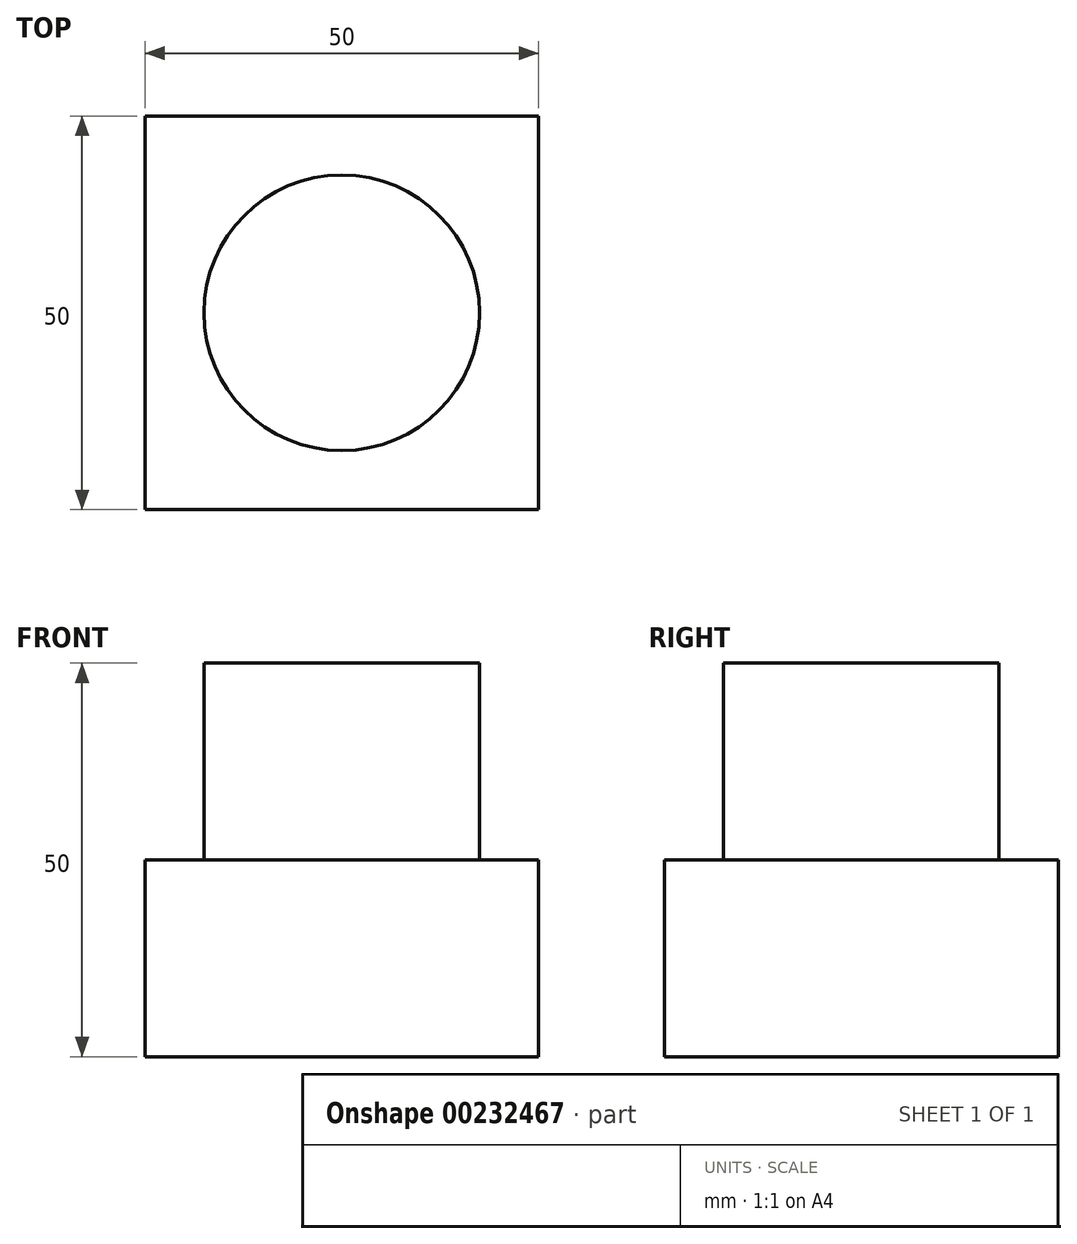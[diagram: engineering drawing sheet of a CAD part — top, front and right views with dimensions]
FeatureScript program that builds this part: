
annotation { "Feature Type Name" : "Feature", "Feature Type Description" : "" }
export const myFeature = defineFeature(function(context is Context, id is Id, definition is map)
    precondition{}
    {
        {
            var Q0;
            Q0=qCreatedBy(makeId("Top.planeOp"),FACE);
            var sketch = newSketch(context, id + "F0", { "sketchPlane" : qUnion([Q0])});
            skLineSegment(sketch, "E0.bottom", {"start": v(-25, -25) * mm, "end": v(25, -25) * mm});
            skLineSegment(sketch, "E0.top", {"start": v(-25, 25) * mm, "end": v(25, 25) * mm});
            skLineSegment(sketch, "E0.left", {"start": v(-25, -25) * mm, "end": v(-25, 25) * mm});
            skLineSegment(sketch, "E0.right", {"start": v(25, -25) * mm, "end": v(25, 25) * mm});
            skPoint(sketch, "E0.middle", {"position": v(0, 0) * mm});
            skSolve(sketch);
        }
        {
            var Q0;
            Q0=makeQuery(id+"F0.imprint","IMPRINT",FACE,{"disambiguationData":[TD([[makeQuery(id+"F0.imprint","IMPRINT",EDGE,{"derivedFrom":sQuery(id+"F0.wireOp",EDGE,"E0.bottom")}),1.0]])]});
            extrude(context, id + "F1", {"entities" : qUnion([Q0]), "depth" : 25 * mm});
        }
        {
            var Q0;
            Q0=makeQuery(id+"F1.opExtrude","CAP_FACE",FACE,{"disambiguationData":[OSD([sQuery(id+"F0.wireOp",EDGE,"E0.bottom"),sQuery(id+"F0.wireOp",EDGE,"E0.top"),sQuery(id+"F0.wireOp",EDGE,"E0.left"),sQuery(id+"F0.wireOp",EDGE,"E0.right")])],"isStart":false});
            var sketch = newSketch(context, id + "F2", { "sketchPlane" : qUnion([Q0])});
            skPoint(sketch, "E1", {"position": v(0, 0) * mm});
            skCircle(sketch, "E2", {"center": v(0, 0) * mm, "radius": 17.5 * mm});
            skSolve(sketch);
        }
        {
            var Q0;
            Q0=makeQuery(id+"F2.imprint","IMPRINT",FACE,{"disambiguationData":[TD([[makeQuery(id+"F2.imprint","IMPRINT",EDGE,{"derivedFrom":sQuery(id+"F2.wireOp",EDGE,"E2")}),1.0]])]});
            extrude(context, id + "F3", {"entities" : qUnion([Q0]), "operationType" : NewBodyOperationType.ADD, "depth" : 25 * mm});
        }
    });
